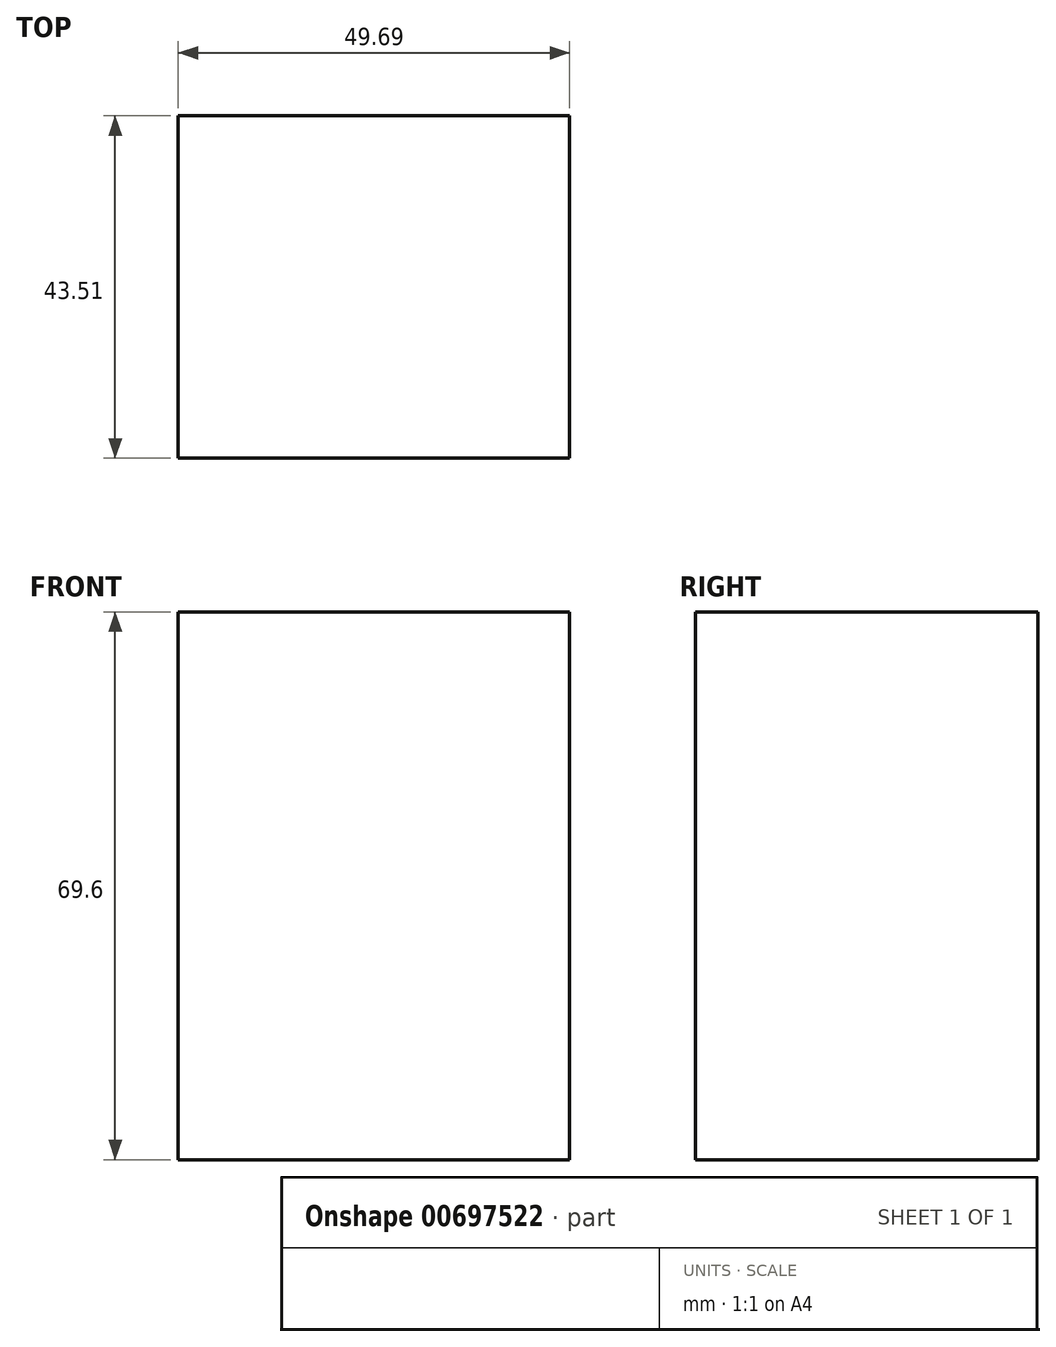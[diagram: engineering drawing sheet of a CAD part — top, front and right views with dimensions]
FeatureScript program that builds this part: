
annotation { "Feature Type Name" : "Feature", "Feature Type Description" : "" }
export const myFeature = defineFeature(function(context is Context, id is Id, definition is map)
    precondition{}
    {
        {
            var Q0;
            Q0=qCreatedBy(makeId("Top.planeOp"),FACE);
            var sketch = newSketch(context, id + "F0", { "sketchPlane" : qUnion([Q0])});
            skLineSegment(sketch, "E0.bottom", {"start": v(-24, 27.93) * mm, "end": v(25.69, 27.93) * mm});
            skLineSegment(sketch, "E0.top", {"start": v(-24, -15.58) * mm, "end": v(25.69, -15.58) * mm});
            skLineSegment(sketch, "E0.left", {"start": v(-24, 27.93) * mm, "end": v(-24, -15.58) * mm});
            skLineSegment(sketch, "E0.right", {"start": v(25.69, 27.93) * mm, "end": v(25.69, -15.58) * mm});
            skSolve(sketch);
        }
        {
            var Q0;
            Q0 = qSketchRegion(id + "F0", true);
            extrude(context, id + "F1", {"entities" : qUnion([Q0]), "depth" : 69.6 * mm, "offsetDistance" : 25.4 * mm});
        }
    });
